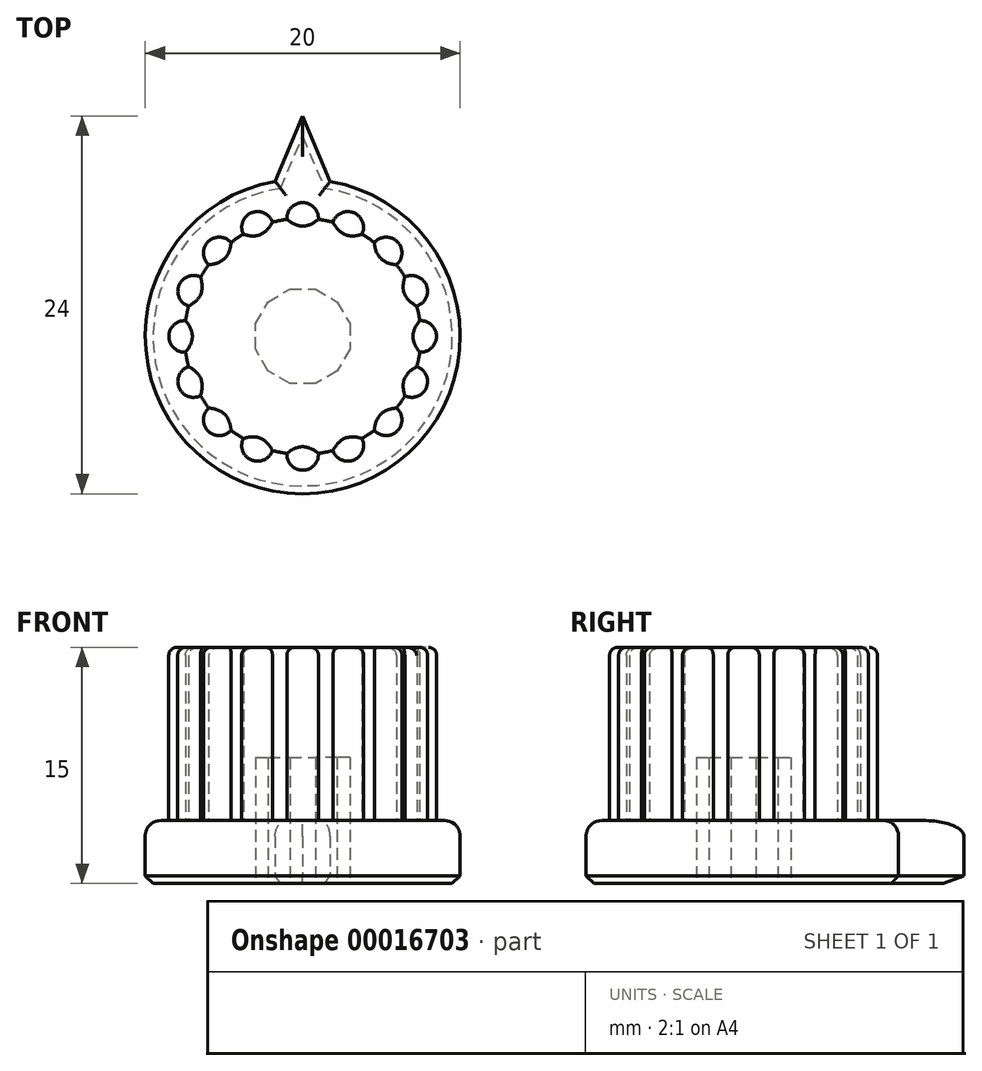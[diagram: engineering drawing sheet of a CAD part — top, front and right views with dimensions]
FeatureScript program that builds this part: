
annotation { "Feature Type Name" : "Feature", "Feature Type Description" : "" }
export const myFeature = defineFeature(function(context is Context, id is Id, definition is map)
    precondition{}
    {
        {
            var Q0;
            Q0=qCreatedBy(makeId("Top.planeOp"),FACE);
            var sketch = newSketch(context, id + "F0", { "sketchPlane" : qUnion([Q0])});
            skCircle(sketch, "E0", {"center": v(0, 0) * mm, "radius": 7.5 * mm});
            skCircle(sketch, "E1", {"center": v(0, 0) * mm, "radius": 10 * mm});
            skCircle(sketch, "E2", {"center": v(0, 0) * mm, "radius": 3 * mm, "construction": true});
            skCircle(sketch, "E3", {"center": v(0, 7.5) * mm, "radius": 1 * mm});
            skCircle(sketch, "E4.1.0", {"center": v(2.87, 6.93) * mm, "radius": 1 * mm});
            skCircle(sketch, "E4.2.0", {"center": v(5.3, 5.3) * mm, "radius": 1 * mm});
            skCircle(sketch, "E4.3.0", {"center": v(6.93, 2.87) * mm, "radius": 1 * mm});
            skCircle(sketch, "E4.4.0", {"center": v(7.5, 0) * mm, "radius": 1 * mm});
            skCircle(sketch, "E4.5.0", {"center": v(6.93, -2.87) * mm, "radius": 1 * mm});
            skCircle(sketch, "E4.6.0", {"center": v(5.3, -5.3) * mm, "radius": 1 * mm});
            skCircle(sketch, "E4.7.0", {"center": v(2.87, -6.93) * mm, "radius": 1 * mm});
            skCircle(sketch, "E4.8.0", {"center": v(0, -7.5) * mm, "radius": 1 * mm});
            skCircle(sketch, "E4.9.0", {"center": v(-2.87, -6.93) * mm, "radius": 1 * mm});
            skCircle(sketch, "E4.10.0", {"center": v(-5.3, -5.3) * mm, "radius": 1 * mm});
            skCircle(sketch, "E4.11.0", {"center": v(-6.93, -2.87) * mm, "radius": 1 * mm});
            skCircle(sketch, "E4.12.0", {"center": v(-7.5, 0) * mm, "radius": 1 * mm});
            skCircle(sketch, "E4.13.0", {"center": v(-6.93, 2.87) * mm, "radius": 1 * mm});
            skCircle(sketch, "E4.14.0", {"center": v(-5.3, 5.3) * mm, "radius": 1 * mm});
            skCircle(sketch, "E4.15.0", {"center": v(-2.87, 6.93) * mm, "radius": 1 * mm});
            skLineSegment(sketch, "E4.anchor1", {"start": v(0, 0) * mm, "end": v(0, 7.5) * mm, "construction": true});
            skLineSegment(sketch, "E4.anchor2", {"start": v(0, 0) * mm, "end": v(-2.87, 6.93) * mm, "construction": true});
            skLineSegment(sketch, "E5", {"start": v(0, 10) * mm, "end": v(0, 14) * mm});
            skLineSegment(sketch, "E6", {"start": v(-1.75, 9.85) * mm, "end": v(0, 14) * mm});
            skLineSegment(sketch, "E7.MirrorCS", {"start": v(1.75, 9.85) * mm, "end": v(0, 14) * mm});
            skLineSegment(sketch, "E8.0", {"start": v(-0.8, 3) * mm, "end": v(0.8, 3) * mm});
            skLineSegment(sketch, "E8.1", {"start": v(0.8, 3) * mm, "end": v(2.2, 2.2) * mm});
            skLineSegment(sketch, "E8.2", {"start": v(2.2, 2.2) * mm, "end": v(3, 0.8) * mm});
            skLineSegment(sketch, "E8.3", {"start": v(3, 0.8) * mm, "end": v(3, -0.8) * mm});
            skLineSegment(sketch, "E8.4", {"start": v(3, -0.8) * mm, "end": v(2.2, -2.2) * mm});
            skLineSegment(sketch, "E8.5", {"start": v(2.2, -2.2) * mm, "end": v(0.8, -3) * mm});
            skLineSegment(sketch, "E8.6", {"start": v(0.8, -3) * mm, "end": v(-0.8, -3) * mm});
            skLineSegment(sketch, "E8.7", {"start": v(-0.8, -3) * mm, "end": v(-2.2, -2.2) * mm});
            skLineSegment(sketch, "E8.8", {"start": v(-2.2, -2.2) * mm, "end": v(-3, -0.8) * mm});
            skLineSegment(sketch, "E8.9", {"start": v(-3, -0.8) * mm, "end": v(-3, 0.8) * mm});
            skLineSegment(sketch, "E8.10", {"start": v(-3, 0.8) * mm, "end": v(-2.2, 2.2) * mm});
            skLineSegment(sketch, "E8.11", {"start": v(-2.2, 2.2) * mm, "end": v(-0.8, 3) * mm});
            skPoint(sketch, "E8.0.midPoint", {"position": v(0, 3) * mm});
            skSolve(sketch);
        }
        {
            var Q0;
            Q0=makeQuery(id+"F0.imprint","IMPRINT",FACE,{"disambiguationData":[TD([[makeQuery(id+"F0.imprint","IMPRINT",EDGE,{"derivedFrom":sQuery(id+"F0.wireOp",EDGE,"E2")}),-1.0]])]});
            var Q1;
            {var subQ0=sQuery(id+"F0.wireOp",EDGE,"E4.12.0");var subQ1=sQuery(id+"F0.wireOp",EDGE,"E0");var subQ3=makeQuery(id+"F0.imprint","INTERSECT",VERTEX,{"disambiguationData":[OD(0.0)],"derivedFrom":[subQ1,subQ0]});Q1=makeQuery(id+"F0.imprint","IMPRINT",FACE,{"disambiguationData":[TD([[makeQuery(id+"F0.imprint","IMPRINT",EDGE,{"disambiguationData":[TD([[subQ3,-1.0]])],"derivedFrom":subQ1}),-1.0]])]});}
            var Q2;
            {var subQ0=sQuery(id+"F0.wireOp",EDGE,"E4.13.0");var subQ1=sQuery(id+"F0.wireOp",EDGE,"E0");var subQ3=makeQuery(id+"F0.imprint","INTERSECT",VERTEX,{"disambiguationData":[OD(0.0)],"derivedFrom":[subQ1,subQ0]});Q2=makeQuery(id+"F0.imprint","IMPRINT",FACE,{"disambiguationData":[TD([[makeQuery(id+"F0.imprint","IMPRINT",EDGE,{"disambiguationData":[TD([[subQ3,-1.0]])],"derivedFrom":subQ1}),-1.0]])]});}
            var Q3;
            {var subQ0=sQuery(id+"F0.wireOp",EDGE,"E4.5.0");var subQ1=sQuery(id+"F0.wireOp",EDGE,"E0");var subQ3=makeQuery(id+"F0.imprint","INTERSECT",VERTEX,{"disambiguationData":[OD(0.0)],"derivedFrom":[subQ1,subQ0]});Q3=makeQuery(id+"F0.imprint","IMPRINT",FACE,{"disambiguationData":[TD([[makeQuery(id+"F0.imprint","IMPRINT",EDGE,{"disambiguationData":[TD([[subQ3,-1.0]])],"derivedFrom":subQ1}),1.0]])]});}
            var Q4;
            {var subQ0=sQuery(id+"F0.wireOp",EDGE,"E4.4.0");var subQ1=sQuery(id+"F0.wireOp",EDGE,"E0");var subQ3=makeQuery(id+"F0.imprint","INTERSECT",VERTEX,{"disambiguationData":[OD(0.0)],"derivedFrom":[subQ1,subQ0]});Q4=makeQuery(id+"F0.imprint","IMPRINT",FACE,{"disambiguationData":[TD([[makeQuery(id+"F0.imprint","IMPRINT",EDGE,{"disambiguationData":[TD([[subQ3,1.0]])],"derivedFrom":subQ1}),-1.0]])]});}
            var Q5;
            {var subQ0=sQuery(id+"F0.wireOp",EDGE,"E4.3.0");var subQ1=sQuery(id+"F0.wireOp",EDGE,"E0");var subQ3=makeQuery(id+"F0.imprint","INTERSECT",VERTEX,{"disambiguationData":[OD(0.0)],"derivedFrom":[subQ1,subQ0]});Q5=makeQuery(id+"F0.imprint","IMPRINT",FACE,{"disambiguationData":[TD([[makeQuery(id+"F0.imprint","IMPRINT",EDGE,{"disambiguationData":[TD([[subQ3,-1.0]])],"derivedFrom":subQ1}),1.0]])]});}
            var Q6;
            {var subQ0=sQuery(id+"F0.wireOp",EDGE,"E4.3.0");var subQ1=sQuery(id+"F0.wireOp",EDGE,"E0");var subQ3=makeQuery(id+"F0.imprint","INTERSECT",VERTEX,{"disambiguationData":[OD(0.0)],"derivedFrom":[subQ1,subQ0]});Q6=makeQuery(id+"F0.imprint","IMPRINT",FACE,{"disambiguationData":[TD([[makeQuery(id+"F0.imprint","IMPRINT",EDGE,{"disambiguationData":[TD([[subQ3,-1.0]])],"derivedFrom":subQ1}),-1.0]])]});}
            var Q7;
            {var subQ0=sQuery(id+"F0.wireOp",EDGE,"E4.2.0");var subQ1=sQuery(id+"F0.wireOp",EDGE,"E0");var subQ3=makeQuery(id+"F0.imprint","INTERSECT",VERTEX,{"disambiguationData":[OD(0.0)],"derivedFrom":[subQ1,subQ0]});Q7=makeQuery(id+"F0.imprint","IMPRINT",FACE,{"disambiguationData":[TD([[makeQuery(id+"F0.imprint","IMPRINT",EDGE,{"disambiguationData":[TD([[subQ3,-1.0]])],"derivedFrom":subQ1}),1.0]])]});}
            var Q8;
            {var subQ0=sQuery(id+"F0.wireOp",EDGE,"E4.2.0");var subQ1=sQuery(id+"F0.wireOp",EDGE,"E0");var subQ3=makeQuery(id+"F0.imprint","INTERSECT",VERTEX,{"disambiguationData":[OD(0.0)],"derivedFrom":[subQ1,subQ0]});Q8=makeQuery(id+"F0.imprint","IMPRINT",FACE,{"disambiguationData":[TD([[makeQuery(id+"F0.imprint","IMPRINT",EDGE,{"disambiguationData":[TD([[subQ3,-1.0]])],"derivedFrom":subQ1}),-1.0]])]});}
            var Q9;
            {var subQ0=sQuery(id+"F0.wireOp",EDGE,"E4.1.0");var subQ1=sQuery(id+"F0.wireOp",EDGE,"E0");var subQ3=makeQuery(id+"F0.imprint","INTERSECT",VERTEX,{"disambiguationData":[OD(0.0)],"derivedFrom":[subQ1,subQ0]});Q9=makeQuery(id+"F0.imprint","IMPRINT",FACE,{"disambiguationData":[TD([[makeQuery(id+"F0.imprint","IMPRINT",EDGE,{"disambiguationData":[TD([[subQ3,-1.0]])],"derivedFrom":subQ1}),1.0]])]});}
            var Q10;
            {var subQ0=sQuery(id+"F0.wireOp",EDGE,"E4.1.0");var subQ1=sQuery(id+"F0.wireOp",EDGE,"E0");var subQ3=makeQuery(id+"F0.imprint","INTERSECT",VERTEX,{"disambiguationData":[OD(0.0)],"derivedFrom":[subQ1,subQ0]});Q10=makeQuery(id+"F0.imprint","IMPRINT",FACE,{"disambiguationData":[TD([[makeQuery(id+"F0.imprint","IMPRINT",EDGE,{"disambiguationData":[TD([[subQ3,-1.0]])],"derivedFrom":subQ1}),-1.0]])]});}
            var Q11;
            {var subQ0=sQuery(id+"F0.wireOp",EDGE,"E3");var subQ1=sQuery(id+"F0.wireOp",EDGE,"E0");var subQ3=makeQuery(id+"F0.imprint","INTERSECT",VERTEX,{"disambiguationData":[OD(0.0)],"derivedFrom":[subQ1,subQ0]});Q11=makeQuery(id+"F0.imprint","IMPRINT",FACE,{"disambiguationData":[TD([[makeQuery(id+"F0.imprint","IMPRINT",EDGE,{"disambiguationData":[TD([[subQ3,-1.0]])],"derivedFrom":subQ1}),1.0]])]});}
            var Q12;
            {var subQ0=sQuery(id+"F0.wireOp",EDGE,"E3");var subQ1=sQuery(id+"F0.wireOp",EDGE,"E0");var subQ3=makeQuery(id+"F0.imprint","INTERSECT",VERTEX,{"disambiguationData":[OD(0.0)],"derivedFrom":[subQ1,subQ0]});Q12=makeQuery(id+"F0.imprint","IMPRINT",FACE,{"disambiguationData":[TD([[makeQuery(id+"F0.imprint","IMPRINT",EDGE,{"disambiguationData":[TD([[subQ3,-1.0]])],"derivedFrom":subQ1}),-1.0]])]});}
            var Q13;
            {var subQ0=sQuery(id+"F0.wireOp",EDGE,"E4.15.0");var subQ1=sQuery(id+"F0.wireOp",EDGE,"E0");var subQ3=makeQuery(id+"F0.imprint","INTERSECT",VERTEX,{"disambiguationData":[OD(0.0)],"derivedFrom":[subQ1,subQ0]});Q13=makeQuery(id+"F0.imprint","IMPRINT",FACE,{"disambiguationData":[TD([[makeQuery(id+"F0.imprint","IMPRINT",EDGE,{"disambiguationData":[TD([[subQ3,-1.0]])],"derivedFrom":subQ1}),1.0]])]});}
            var Q14;
            {var subQ0=sQuery(id+"F0.wireOp",EDGE,"E4.15.0");var subQ1=sQuery(id+"F0.wireOp",EDGE,"E0");var subQ3=makeQuery(id+"F0.imprint","INTERSECT",VERTEX,{"disambiguationData":[OD(0.0)],"derivedFrom":[subQ1,subQ0]});Q14=makeQuery(id+"F0.imprint","IMPRINT",FACE,{"disambiguationData":[TD([[makeQuery(id+"F0.imprint","IMPRINT",EDGE,{"disambiguationData":[TD([[subQ3,-1.0]])],"derivedFrom":subQ1}),-1.0]])]});}
            var Q15;
            {var subQ0=sQuery(id+"F0.wireOp",EDGE,"E4.14.0");var subQ1=sQuery(id+"F0.wireOp",EDGE,"E0");var subQ3=makeQuery(id+"F0.imprint","INTERSECT",VERTEX,{"disambiguationData":[OD(0.0)],"derivedFrom":[subQ1,subQ0]});Q15=makeQuery(id+"F0.imprint","IMPRINT",FACE,{"disambiguationData":[TD([[makeQuery(id+"F0.imprint","IMPRINT",EDGE,{"disambiguationData":[TD([[subQ3,-1.0]])],"derivedFrom":subQ1}),1.0]])]});}
            var Q16;
            {var subQ0=sQuery(id+"F0.wireOp",EDGE,"E4.14.0");var subQ1=sQuery(id+"F0.wireOp",EDGE,"E0");var subQ3=makeQuery(id+"F0.imprint","INTERSECT",VERTEX,{"disambiguationData":[OD(0.0)],"derivedFrom":[subQ1,subQ0]});Q16=makeQuery(id+"F0.imprint","IMPRINT",FACE,{"disambiguationData":[TD([[makeQuery(id+"F0.imprint","IMPRINT",EDGE,{"disambiguationData":[TD([[subQ3,-1.0]])],"derivedFrom":subQ1}),-1.0]])]});}
            var Q17;
            {var subQ0=sQuery(id+"F0.wireOp",EDGE,"E4.5.0");var subQ1=sQuery(id+"F0.wireOp",EDGE,"E0");var subQ3=makeQuery(id+"F0.imprint","INTERSECT",VERTEX,{"disambiguationData":[OD(0.0)],"derivedFrom":[subQ1,subQ0]});Q17=makeQuery(id+"F0.imprint","IMPRINT",FACE,{"disambiguationData":[TD([[makeQuery(id+"F0.imprint","IMPRINT",EDGE,{"disambiguationData":[TD([[subQ3,-1.0]])],"derivedFrom":subQ1}),-1.0]])]});}
            var Q18;
            {var subQ0=sQuery(id+"F0.wireOp",EDGE,"E4.4.0");var subQ1=sQuery(id+"F0.wireOp",EDGE,"E0");var subQ3=makeQuery(id+"F0.imprint","INTERSECT",VERTEX,{"disambiguationData":[OD(0.0)],"derivedFrom":[subQ1,subQ0]});Q18=makeQuery(id+"F0.imprint","IMPRINT",FACE,{"disambiguationData":[TD([[makeQuery(id+"F0.imprint","IMPRINT",EDGE,{"disambiguationData":[TD([[subQ3,1.0]])],"derivedFrom":subQ1}),1.0]])]});}
            var Q19;
            {var subQ0=sQuery(id+"F0.wireOp",EDGE,"E4.7.0");var subQ1=sQuery(id+"F0.wireOp",EDGE,"E0");var subQ3=makeQuery(id+"F0.imprint","INTERSECT",VERTEX,{"disambiguationData":[OD(0.0)],"derivedFrom":[subQ1,subQ0]});Q19=makeQuery(id+"F0.imprint","IMPRINT",FACE,{"disambiguationData":[TD([[makeQuery(id+"F0.imprint","IMPRINT",EDGE,{"disambiguationData":[TD([[subQ3,-1.0]])],"derivedFrom":subQ1}),-1.0]])]});}
            var Q20;
            {var subQ0=sQuery(id+"F0.wireOp",EDGE,"E4.12.0");var subQ1=sQuery(id+"F0.wireOp",EDGE,"E0");var subQ3=makeQuery(id+"F0.imprint","INTERSECT",VERTEX,{"disambiguationData":[OD(0.0)],"derivedFrom":[subQ1,subQ0]});Q20=makeQuery(id+"F0.imprint","IMPRINT",FACE,{"disambiguationData":[TD([[makeQuery(id+"F0.imprint","IMPRINT",EDGE,{"disambiguationData":[TD([[subQ3,-1.0]])],"derivedFrom":subQ1}),1.0]])]});}
            var Q21;
            {var subQ0=sQuery(id+"F0.wireOp",EDGE,"E4.10.0");var subQ1=sQuery(id+"F0.wireOp",EDGE,"E0");var subQ3=makeQuery(id+"F0.imprint","INTERSECT",VERTEX,{"disambiguationData":[OD(0.0)],"derivedFrom":[subQ1,subQ0]});Q21=makeQuery(id+"F0.imprint","IMPRINT",FACE,{"disambiguationData":[TD([[makeQuery(id+"F0.imprint","IMPRINT",EDGE,{"disambiguationData":[TD([[subQ3,-1.0]])],"derivedFrom":subQ1}),-1.0]])]});}
            var Q22;
            {var subQ0=sQuery(id+"F0.wireOp",EDGE,"E4.10.0");var subQ1=sQuery(id+"F0.wireOp",EDGE,"E0");var subQ3=makeQuery(id+"F0.imprint","INTERSECT",VERTEX,{"disambiguationData":[OD(0.0)],"derivedFrom":[subQ1,subQ0]});Q22=makeQuery(id+"F0.imprint","IMPRINT",FACE,{"disambiguationData":[TD([[makeQuery(id+"F0.imprint","IMPRINT",EDGE,{"disambiguationData":[TD([[subQ3,-1.0]])],"derivedFrom":subQ1}),1.0]])]});}
            var Q23;
            {var subQ0=sQuery(id+"F0.wireOp",EDGE,"E4.9.0");var subQ1=sQuery(id+"F0.wireOp",EDGE,"E0");var subQ3=makeQuery(id+"F0.imprint","INTERSECT",VERTEX,{"disambiguationData":[OD(0.0)],"derivedFrom":[subQ1,subQ0]});Q23=makeQuery(id+"F0.imprint","IMPRINT",FACE,{"disambiguationData":[TD([[makeQuery(id+"F0.imprint","IMPRINT",EDGE,{"disambiguationData":[TD([[subQ3,-1.0]])],"derivedFrom":subQ1}),-1.0]])]});}
            var Q24;
            {var subQ0=sQuery(id+"F0.wireOp",EDGE,"E4.13.0");var subQ1=sQuery(id+"F0.wireOp",EDGE,"E0");var subQ3=makeQuery(id+"F0.imprint","INTERSECT",VERTEX,{"disambiguationData":[OD(0.0)],"derivedFrom":[subQ1,subQ0]});Q24=makeQuery(id+"F0.imprint","IMPRINT",FACE,{"disambiguationData":[TD([[makeQuery(id+"F0.imprint","IMPRINT",EDGE,{"disambiguationData":[TD([[subQ3,-1.0]])],"derivedFrom":subQ1}),1.0]])]});}
            var Q25;
            {var subQ0=sQuery(id+"F0.wireOp",EDGE,"E4.6.0");var subQ1=sQuery(id+"F0.wireOp",EDGE,"E0");var subQ3=makeQuery(id+"F0.imprint","INTERSECT",VERTEX,{"disambiguationData":[OD(0.0)],"derivedFrom":[subQ1,subQ0]});Q25=makeQuery(id+"F0.imprint","IMPRINT",FACE,{"disambiguationData":[TD([[makeQuery(id+"F0.imprint","IMPRINT",EDGE,{"disambiguationData":[TD([[subQ3,-1.0]])],"derivedFrom":subQ1}),1.0]])]});}
            var Q26;
            {var subQ0=sQuery(id+"F0.wireOp",EDGE,"E4.8.0");var subQ1=sQuery(id+"F0.wireOp",EDGE,"E0");var subQ3=makeQuery(id+"F0.imprint","INTERSECT",VERTEX,{"disambiguationData":[OD(0.0)],"derivedFrom":[subQ1,subQ0]});Q26=makeQuery(id+"F0.imprint","IMPRINT",FACE,{"disambiguationData":[TD([[makeQuery(id+"F0.imprint","IMPRINT",EDGE,{"disambiguationData":[TD([[subQ3,-1.0]])],"derivedFrom":subQ1}),1.0]])]});}
            var Q27;
            {var subQ0=sQuery(id+"F0.wireOp",EDGE,"E4.9.0");var subQ1=sQuery(id+"F0.wireOp",EDGE,"E0");var subQ3=makeQuery(id+"F0.imprint","INTERSECT",VERTEX,{"disambiguationData":[OD(0.0)],"derivedFrom":[subQ1,subQ0]});Q27=makeQuery(id+"F0.imprint","IMPRINT",FACE,{"disambiguationData":[TD([[makeQuery(id+"F0.imprint","IMPRINT",EDGE,{"disambiguationData":[TD([[subQ3,-1.0]])],"derivedFrom":subQ1}),1.0]])]});}
            var Q28;
            {var subQ0=sQuery(id+"F0.wireOp",EDGE,"E4.11.0");var subQ1=sQuery(id+"F0.wireOp",EDGE,"E0");var subQ3=makeQuery(id+"F0.imprint","INTERSECT",VERTEX,{"disambiguationData":[OD(0.0)],"derivedFrom":[subQ1,subQ0]});Q28=makeQuery(id+"F0.imprint","IMPRINT",FACE,{"disambiguationData":[TD([[makeQuery(id+"F0.imprint","IMPRINT",EDGE,{"disambiguationData":[TD([[subQ3,-1.0]])],"derivedFrom":subQ1}),1.0]])]});}
            var Q29;
            {var subQ0=sQuery(id+"F0.wireOp",EDGE,"E4.6.0");var subQ1=sQuery(id+"F0.wireOp",EDGE,"E0");var subQ3=makeQuery(id+"F0.imprint","INTERSECT",VERTEX,{"disambiguationData":[OD(0.0)],"derivedFrom":[subQ1,subQ0]});Q29=makeQuery(id+"F0.imprint","IMPRINT",FACE,{"disambiguationData":[TD([[makeQuery(id+"F0.imprint","IMPRINT",EDGE,{"disambiguationData":[TD([[subQ3,-1.0]])],"derivedFrom":subQ1}),-1.0]])]});}
            var Q30;
            {var subQ0=sQuery(id+"F0.wireOp",EDGE,"E4.8.0");var subQ1=sQuery(id+"F0.wireOp",EDGE,"E0");var subQ3=makeQuery(id+"F0.imprint","INTERSECT",VERTEX,{"disambiguationData":[OD(0.0)],"derivedFrom":[subQ1,subQ0]});Q30=makeQuery(id+"F0.imprint","IMPRINT",FACE,{"disambiguationData":[TD([[makeQuery(id+"F0.imprint","IMPRINT",EDGE,{"disambiguationData":[TD([[subQ3,-1.0]])],"derivedFrom":subQ1}),-1.0]])]});}
            var Q31;
            {var subQ0=sQuery(id+"F0.wireOp",EDGE,"E4.11.0");var subQ1=sQuery(id+"F0.wireOp",EDGE,"E0");var subQ3=makeQuery(id+"F0.imprint","INTERSECT",VERTEX,{"disambiguationData":[OD(0.0)],"derivedFrom":[subQ1,subQ0]});Q31=makeQuery(id+"F0.imprint","IMPRINT",FACE,{"disambiguationData":[TD([[makeQuery(id+"F0.imprint","IMPRINT",EDGE,{"disambiguationData":[TD([[subQ3,-1.0]])],"derivedFrom":subQ1}),-1.0]])]});}
            var Q32;
            {var subQ0=sQuery(id+"F0.wireOp",EDGE,"E4.7.0");var subQ1=sQuery(id+"F0.wireOp",EDGE,"E0");var subQ3=makeQuery(id+"F0.imprint","INTERSECT",VERTEX,{"disambiguationData":[OD(0.0)],"derivedFrom":[subQ1,subQ0]});Q32=makeQuery(id+"F0.imprint","IMPRINT",FACE,{"disambiguationData":[TD([[makeQuery(id+"F0.imprint","IMPRINT",EDGE,{"disambiguationData":[TD([[subQ3,-1.0]])],"derivedFrom":subQ1}),1.0]])]});}
            var Q33;
            Q33=makeQuery(id+"F0.imprint","IMPRINT",FACE,{"disambiguationData":[TD([[makeQuery(id+"F0.imprint","IMPRINT",EDGE,{"derivedFrom":sQuery(id+"F0.wireOp",EDGE,"E2")}),1.0]])]});
            var Q34;
            Q34=makeQuery(id+"F0.imprint","IMPRINT",FACE,{"disambiguationData":[TD([[makeQuery(id+"F0.imprint","IMPRINT",EDGE,{"derivedFrom":sQuery(id+"F0.wireOp",EDGE,"E8.0")}),1.0]])]});
            var Q35;
            Q35=makeQuery(id+"F0.imprint","IMPRINT",FACE,{"disambiguationData":[TD([[makeQuery(id+"F0.imprint","IMPRINT",EDGE,{"derivedFrom":sQuery(id+"F0.wireOp",EDGE,"E8.0")}),-1.0]])]});
            extrude(context, id + "F1", {"entities" : qUnion([Q0, Q1, Q2, Q3, Q4, Q5, Q6, Q7, Q8, Q9, Q10, Q11, Q12, Q13, Q14, Q15, Q16, Q17, Q18, Q19, Q20, Q21, Q22, Q23, Q24, Q25, Q26, Q27, Q28, Q29, Q30, Q31, Q32, Q33, Q34, Q35]), "depth" : 15 * mm});
        }
        {
            var Q0;
            Q0=makeQuery(id+"F0.imprint","IMPRINT",FACE,{"disambiguationData":[TD([[makeQuery(id+"F0.imprint","IMPRINT",EDGE,{"derivedFrom":sQuery(id+"F0.wireOp",EDGE,"E1")}),1.0]])]});
            var Q1;
            {var subQ1=sQuery(id+"F0.wireOp",EDGE,"E5");Q1=makeQuery(id+"F0.imprint","IMPRINT",FACE,{"disambiguationData":[TD([[makeQuery(id+"F0.imprint","IMPRINT",EDGE,{"derivedFrom":subQ1}),-1.0]])]});}
            var Q2;
            {var subQ1=sQuery(id+"F0.wireOp",EDGE,"E5");Q2=makeQuery(id+"F0.imprint","IMPRINT",FACE,{"disambiguationData":[TD([[makeQuery(id+"F0.imprint","IMPRINT",EDGE,{"derivedFrom":subQ1}),1.0]])]});}
            extrude(context, id + "F2", {"entities" : qUnion([Q0, Q1, Q2]), "operationType" : NewBodyOperationType.ADD, "depth" : 4 * mm});
        }
        {
            var Q0;
            Q0=makeQuery(id+"F0.imprint","IMPRINT",FACE,{"disambiguationData":[TD([[makeQuery(id+"F0.imprint","IMPRINT",EDGE,{"derivedFrom":sQuery(id+"F0.wireOp",EDGE,"E8.0")}),-1.0]])]});
            extrude(context, id + "F3", {"entities" : qUnion([Q0]), "operationType" : NewBodyOperationType.REMOVE, "depth" : 8 * mm});
        }
        {
            var Q0;
            Q0=makeQuery(id+"F2.opExtrude","CAP_EDGE",EDGE,{"disambiguationData":[OSD([sQuery(id+"F0.wireOp",EDGE,"E1")])],"isStart":false});
            var Q1;
            Q1=makeQuery(id+"F2.opExtrude","CAP_EDGE",EDGE,{"disambiguationData":[OSD([sQuery(id+"F0.wireOp",EDGE,"be9af46f-8be3-4fce-9193-26453e98453a")])],"isStart":false});
            var Q2;
            Q2=makeQuery(id+"F2.opExtrude","CAP_EDGE",EDGE,{"disambiguationData":[OSD([sQuery(id+"F0.wireOp",EDGE,"E6")])],"isStart":false});
            var Q3;
            Q3=makeQuery(id+"F2.opExtrude","CAP_EDGE",EDGE,{"disambiguationData":[OSD([sQuery(id+"F0.wireOp",EDGE,"E7.MirrorCS")])],"isStart":false});
            fillet(context, id + "F4", {"entities" : qUnion([Q0, Q1, Q2, Q3]), "radius" : 1 * mm, "tangentPropagation" : true, "allowEdgeOverflow" : false});
        }
        {
            var Q0;
            Q0=makeQuery(id+"F2.opExtrude","CAP_EDGE",EDGE,{"disambiguationData":[OSD([sQuery(id+"F0.wireOp",EDGE,"E1")])],"isStart":true});
            var Q1;
            Q1=makeQuery(id+"F2.opExtrude","CAP_EDGE",EDGE,{"disambiguationData":[OSD([sQuery(id+"F0.wireOp",EDGE,"E6")])],"isStart":true});
            var Q2;
            Q2=makeQuery(id+"F2.opExtrude","CAP_EDGE",EDGE,{"disambiguationData":[OSD([sQuery(id+"F0.wireOp",EDGE,"be9af46f-8be3-4fce-9193-26453e98453a")])],"isStart":true});
            var Q3;
            Q3=makeQuery(id+"F2.opExtrude","CAP_EDGE",EDGE,{"disambiguationData":[OSD([sQuery(id+"F0.wireOp",EDGE,"E7.MirrorCS")])],"isStart":true});
            chamfer(context, id + "F5", {"entities" : qUnion([Q0, Q1, Q2, Q3]), "width" : 0.5 * mm, "tangentPropagation" : true});
        }
        {
            var Q0;
            Q0=makeQuery(id+"F1.opExtrude","CAP_EDGE",EDGE,{"disambiguationData":[OSD([sQuery(id+"F0.wireOp",EDGE,"E4.12.0")])],"isStart":false});
            var Q1;
            Q1=makeQuery(id+"F1.opExtrude","CAP_EDGE",EDGE,{"disambiguationData":[OSD([sQuery(id+"F0.wireOp",EDGE,"E4.5.0")])],"isStart":false});
            var Q2;
            Q2=makeQuery(id+"F1.opExtrude","CAP_EDGE",EDGE,{"disambiguationData":[OSD([sQuery(id+"F0.wireOp",EDGE,"E4.10.0")])],"isStart":false});
            var Q3;
            {var subQ0=sQuery(id+"F0.wireOp",EDGE,"E0");Q3=makeQuery(id+"F1.opExtrude","CAP_EDGE",EDGE,{"disambiguationData":[OSD([subQ0]),TDD([makeQuery(id+"F0.imprint","IMPRINT",EDGE,{"disambiguationData":[TD([[makeQuery(id+"F0.imprint","INTERSECT",VERTEX,{"disambiguationData":[OD(1.0)],"derivedFrom":[subQ0,sQuery(id+"F0.wireOp",EDGE,"E4.2.0")]}),-1.0]])],"derivedFrom":subQ0})])],"isStart":false});}
            var Q4;
            Q4=makeQuery(id+"F1.opExtrude","CAP_EDGE",EDGE,{"disambiguationData":[OSD([sQuery(id+"F0.wireOp",EDGE,"E4.6.0")])],"isStart":false});
            var Q5;
            Q5=makeQuery(id+"F1.opExtrude","CAP_EDGE",EDGE,{"disambiguationData":[OSD([sQuery(id+"F0.wireOp",EDGE,"E4.11.0")])],"isStart":false});
            var Q6;
            Q6=makeQuery(id+"F1.opExtrude","CAP_EDGE",EDGE,{"disambiguationData":[OSD([sQuery(id+"F0.wireOp",EDGE,"E4.13.0")])],"isStart":false});
            var Q7;
            Q7=makeQuery(id+"F1.opExtrude","CAP_EDGE",EDGE,{"disambiguationData":[OSD([sQuery(id+"F0.wireOp",EDGE,"E4.4.0")])],"isStart":false});
            var Q8;
            {var subQ0=sQuery(id+"F0.wireOp",EDGE,"E0");Q8=makeQuery(id+"F1.opExtrude","CAP_EDGE",EDGE,{"disambiguationData":[OSD([subQ0]),TDD([makeQuery(id+"F0.imprint","IMPRINT",EDGE,{"disambiguationData":[TD([[makeQuery(id+"F0.imprint","INTERSECT",VERTEX,{"disambiguationData":[OD(1.0)],"derivedFrom":[subQ0,sQuery(id+"F0.wireOp",EDGE,"E4.8.0")]}),-1.0]])],"derivedFrom":subQ0})])],"isStart":false});}
            var Q9;
            {var subQ0=sQuery(id+"F0.wireOp",EDGE,"E0");Q9=makeQuery(id+"F1.opExtrude","CAP_EDGE",EDGE,{"disambiguationData":[OSD([subQ0]),TDD([makeQuery(id+"F0.imprint","IMPRINT",EDGE,{"disambiguationData":[TD([[makeQuery(id+"F0.imprint","INTERSECT",VERTEX,{"disambiguationData":[OD(1.0)],"derivedFrom":[subQ0,sQuery(id+"F0.wireOp",EDGE,"E4.15.0")]}),-1.0]])],"derivedFrom":subQ0})])],"isStart":false});}
            var Q10;
            Q10=makeQuery(id+"F1.opExtrude","CAP_EDGE",EDGE,{"disambiguationData":[OSD([sQuery(id+"F0.wireOp",EDGE,"E4.15.0")])],"isStart":false});
            var Q11;
            {var subQ0=sQuery(id+"F0.wireOp",EDGE,"E0");Q11=makeQuery(id+"F1.opExtrude","CAP_EDGE",EDGE,{"disambiguationData":[OSD([subQ0]),TDD([makeQuery(id+"F0.imprint","IMPRINT",EDGE,{"disambiguationData":[TD([[makeQuery(id+"F0.imprint","INTERSECT",VERTEX,{"disambiguationData":[OD(1.0)],"derivedFrom":[subQ0,sQuery(id+"F0.wireOp",EDGE,"E4.13.0")]}),-1.0]])],"derivedFrom":subQ0})])],"isStart":false});}
            var Q12;
            Q12=makeQuery(id+"F1.opExtrude","CAP_EDGE",EDGE,{"disambiguationData":[OSD([sQuery(id+"F0.wireOp",EDGE,"E4.2.0")])],"isStart":false});
            var Q13;
            {var subQ0=sQuery(id+"F0.wireOp",EDGE,"E0");Q13=makeQuery(id+"F1.opExtrude","CAP_EDGE",EDGE,{"disambiguationData":[OSD([subQ0]),TDD([makeQuery(id+"F0.imprint","IMPRINT",EDGE,{"disambiguationData":[TD([[makeQuery(id+"F0.imprint","INTERSECT",VERTEX,{"disambiguationData":[OD(1.0)],"derivedFrom":[subQ0,sQuery(id+"F0.wireOp",EDGE,"E4.9.0")]}),-1.0]])],"derivedFrom":subQ0})])],"isStart":false});}
            var Q14;
            {var subQ0=sQuery(id+"F0.wireOp",EDGE,"E0");Q14=makeQuery(id+"F1.opExtrude","CAP_EDGE",EDGE,{"disambiguationData":[OSD([subQ0]),TDD([makeQuery(id+"F0.imprint","IMPRINT",EDGE,{"disambiguationData":[TD([[makeQuery(id+"F0.imprint","INTERSECT",VERTEX,{"disambiguationData":[OD(1.0)],"derivedFrom":[subQ0,sQuery(id+"F0.wireOp",EDGE,"E4.10.0")]}),-1.0]])],"derivedFrom":subQ0})])],"isStart":false});}
            var Q15;
            Q15=makeQuery(id+"F1.opExtrude","CAP_EDGE",EDGE,{"disambiguationData":[OSD([sQuery(id+"F0.wireOp",EDGE,"E3")])],"isStart":false});
            var Q16;
            {var subQ0=sQuery(id+"F0.wireOp",EDGE,"E0");Q16=makeQuery(id+"F1.opExtrude","CAP_EDGE",EDGE,{"disambiguationData":[OSD([subQ0]),TDD([makeQuery(id+"F0.imprint","IMPRINT",EDGE,{"disambiguationData":[TD([[makeQuery(id+"F0.imprint","INTERSECT",VERTEX,{"disambiguationData":[OD(1.0)],"derivedFrom":[subQ0,sQuery(id+"F0.wireOp",EDGE,"E4.12.0")]}),-1.0]])],"derivedFrom":subQ0})])],"isStart":false});}
            var Q17;
            Q17=makeQuery(id+"F1.opExtrude","CAP_EDGE",EDGE,{"disambiguationData":[OSD([sQuery(id+"F0.wireOp",EDGE,"E4.8.0")])],"isStart":false});
            var Q18;
            {var subQ0=sQuery(id+"F0.wireOp",EDGE,"E0");Q18=makeQuery(id+"F1.opExtrude","CAP_EDGE",EDGE,{"disambiguationData":[OSD([subQ0]),TDD([makeQuery(id+"F0.imprint","IMPRINT",EDGE,{"disambiguationData":[TD([[makeQuery(id+"F0.imprint","INTERSECT",VERTEX,{"disambiguationData":[OD(1.0)],"derivedFrom":[subQ0,sQuery(id+"F0.wireOp",EDGE,"E4.6.0")]}),-1.0]])],"derivedFrom":subQ0})])],"isStart":false});}
            var Q19;
            Q19=makeQuery(id+"F1.opExtrude","CAP_EDGE",EDGE,{"disambiguationData":[OSD([sQuery(id+"F0.wireOp",EDGE,"E4.14.0")])],"isStart":false});
            var Q20;
            {var subQ0=sQuery(id+"F0.wireOp",EDGE,"E0");Q20=makeQuery(id+"F1.opExtrude","CAP_EDGE",EDGE,{"disambiguationData":[OSD([subQ0]),TDD([makeQuery(id+"F0.imprint","IMPRINT",EDGE,{"disambiguationData":[TD([[makeQuery(id+"F0.imprint","INTERSECT",VERTEX,{"disambiguationData":[OD(1.0)],"derivedFrom":[subQ0,sQuery(id+"F0.wireOp",EDGE,"E4.1.0")]}),-1.0]])],"derivedFrom":subQ0})])],"isStart":false});}
            var Q21;
            Q21=makeQuery(id+"F1.opExtrude","CAP_EDGE",EDGE,{"disambiguationData":[OSD([sQuery(id+"F0.wireOp",EDGE,"E4.3.0")])],"isStart":false});
            var Q22;
            {var subQ0=sQuery(id+"F0.wireOp",EDGE,"E0");Q22=makeQuery(id+"F1.opExtrude","CAP_EDGE",EDGE,{"disambiguationData":[OSD([subQ0]),TDD([makeQuery(id+"F0.imprint","IMPRINT",EDGE,{"disambiguationData":[TD([[makeQuery(id+"F0.imprint","INTERSECT",VERTEX,{"disambiguationData":[OD(1.0)],"derivedFrom":[subQ0,sQuery(id+"F0.wireOp",EDGE,"E4.14.0")]}),-1.0]])],"derivedFrom":subQ0})])],"isStart":false});}
            var Q23;
            {var subQ0=sQuery(id+"F0.wireOp",EDGE,"E0");Q23=makeQuery(id+"F1.opExtrude","CAP_EDGE",EDGE,{"disambiguationData":[OSD([subQ0]),TDD([makeQuery(id+"F0.imprint","IMPRINT",EDGE,{"disambiguationData":[TD([[makeQuery(id+"F0.imprint","INTERSECT",VERTEX,{"disambiguationData":[OD(1.0)],"derivedFrom":[subQ0,sQuery(id+"F0.wireOp",EDGE,"E4.7.0")]}),-1.0]])],"derivedFrom":subQ0})])],"isStart":false});}
            var Q24;
            {var subQ0=sQuery(id+"F0.wireOp",EDGE,"E0");Q24=makeQuery(id+"F1.opExtrude","CAP_EDGE",EDGE,{"disambiguationData":[OSD([subQ0]),TDD([makeQuery(id+"F0.imprint","IMPRINT",EDGE,{"disambiguationData":[TD([[makeQuery(id+"F0.imprint","INTERSECT",VERTEX,{"disambiguationData":[OD(1.0)],"derivedFrom":[subQ0,sQuery(id+"F0.wireOp",EDGE,"E3")]}),-1.0]])],"derivedFrom":subQ0})])],"isStart":false});}
            var Q25;
            {var subQ0=sQuery(id+"F0.wireOp",EDGE,"E0");Q25=makeQuery(id+"F1.opExtrude","CAP_EDGE",EDGE,{"disambiguationData":[OSD([subQ0]),TDD([makeQuery(id+"F0.imprint","IMPRINT",EDGE,{"disambiguationData":[TD([[makeQuery(id+"F0.imprint","INTERSECT",VERTEX,{"disambiguationData":[OD(0.0)],"derivedFrom":[subQ0,sQuery(id+"F0.wireOp",EDGE,"E4.3.0")]}),1.0]])],"derivedFrom":subQ0})])],"isStart":false});}
            var Q26;
            {var subQ0=sQuery(id+"F0.wireOp",EDGE,"E0");Q26=makeQuery(id+"F1.opExtrude","CAP_EDGE",EDGE,{"disambiguationData":[OSD([subQ0]),TDD([makeQuery(id+"F0.imprint","IMPRINT",EDGE,{"disambiguationData":[TD([[makeQuery(id+"F0.imprint","INTERSECT",VERTEX,{"disambiguationData":[OD(1.0)],"derivedFrom":[subQ0,sQuery(id+"F0.wireOp",EDGE,"E4.5.0")]}),-1.0]])],"derivedFrom":subQ0})])],"isStart":false});}
            var Q27;
            Q27=makeQuery(id+"F1.opExtrude","CAP_EDGE",EDGE,{"disambiguationData":[OSD([sQuery(id+"F0.wireOp",EDGE,"E4.7.0")])],"isStart":false});
            var Q28;
            {var subQ0=sQuery(id+"F0.wireOp",EDGE,"E0");Q28=makeQuery(id+"F1.opExtrude","CAP_EDGE",EDGE,{"disambiguationData":[OSD([subQ0]),TDD([makeQuery(id+"F0.imprint","IMPRINT",EDGE,{"disambiguationData":[TD([[makeQuery(id+"F0.imprint","INTERSECT",VERTEX,{"disambiguationData":[OD(1.0)],"derivedFrom":[subQ0,sQuery(id+"F0.wireOp",EDGE,"E4.11.0")]}),-1.0]])],"derivedFrom":subQ0})])],"isStart":false});}
            var Q29;
            {var subQ0=sQuery(id+"F0.wireOp",EDGE,"E0");Q29=makeQuery(id+"F1.opExtrude","CAP_EDGE",EDGE,{"disambiguationData":[OSD([subQ0]),TDD([makeQuery(id+"F0.imprint","IMPRINT",EDGE,{"disambiguationData":[TD([[makeQuery(id+"F0.imprint","INTERSECT",VERTEX,{"disambiguationData":[OD(1.0)],"derivedFrom":[subQ0,sQuery(id+"F0.wireOp",EDGE,"E4.3.0")]}),-1.0]])],"derivedFrom":subQ0})])],"isStart":false});}
            var Q30;
            Q30=makeQuery(id+"F1.opExtrude","CAP_EDGE",EDGE,{"disambiguationData":[OSD([sQuery(id+"F0.wireOp",EDGE,"E4.9.0")])],"isStart":false});
            var Q31;
            Q31=makeQuery(id+"F1.opExtrude","CAP_EDGE",EDGE,{"disambiguationData":[OSD([sQuery(id+"F0.wireOp",EDGE,"E4.1.0")])],"isStart":false});
            fillet(context, id + "F6", {"entities" : qUnion([Q0, Q1, Q2, Q3, Q4, Q5, Q6, Q7, Q8, Q9, Q10, Q11, Q12, Q13, Q14, Q15, Q16, Q17, Q18, Q19, Q20, Q21, Q22, Q23, Q24, Q25, Q26, Q27, Q28, Q29, Q30, Q31]), "radius" : 0.5 * mm, "allowEdgeOverflow" : false});
        }
    });
